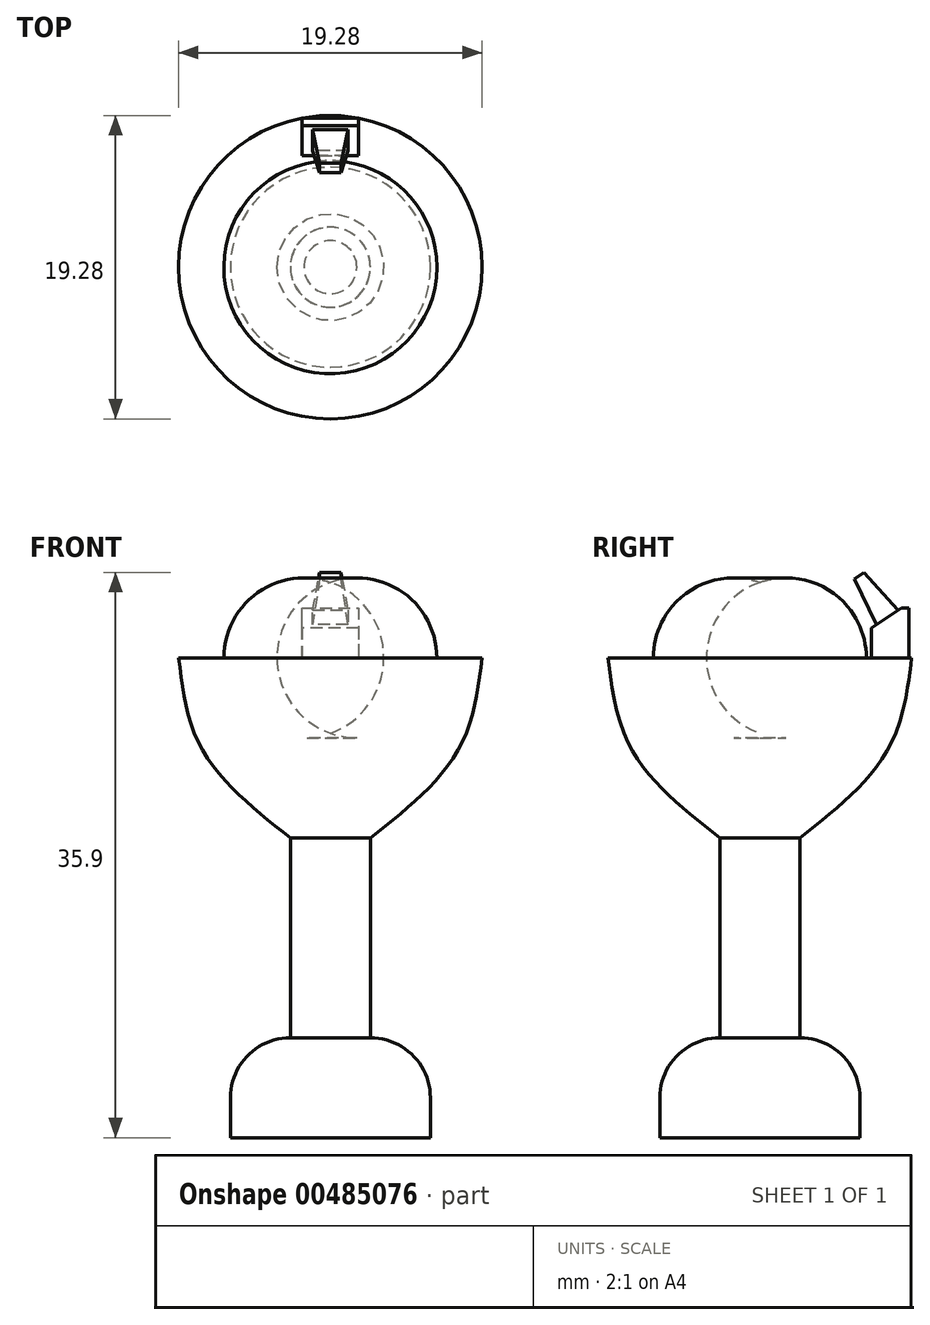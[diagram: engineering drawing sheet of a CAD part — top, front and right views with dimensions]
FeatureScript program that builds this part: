
annotation { "Feature Type Name" : "Feature", "Feature Type Description" : "" }
export const myFeature = defineFeature(function(context is Context, id is Id, definition is map)
    precondition{}
    {
        {
            var Q0;
            Q0=qCreatedBy(makeId("Top.planeOp"),FACE);
            var sketch = newSketch(context, id + "F0", { "sketchPlane" : qUnion([Q0])});
            skCircle(sketch, "E0", {"center": v(0, 0) * mm, "radius": 6.35 * mm});
            skSolve(sketch);
        }
        {
            var Q0;
            Q0 = qSketchRegion(id + "F0", true);
            extrude(context, id + "F1", {"entities" : qUnion([Q0]), "depth" : 6.35 * mm});
        }
        {
            var Q0;
            Q0=makeQuery(id+"F1.opExtrude","CAP_EDGE",EDGE,{"disambiguationData":[OSD([sQuery(id+"F0.wireOp",EDGE,"E0")])],"isStart":false});
            fillet(context, id + "F2", {"entities" : qUnion([Q0]), "radius" : 3.8 * mm, "tangentPropagation" : true, "allowEdgeOverflow" : false});
        }
        {
            var Q0;
            Q0=makeQuery(id+"F1.opExtrude","CAP_FACE",FACE,{"disambiguationData":[OSD([sQuery(id+"F0.wireOp",EDGE,"E0")])],"isStart":false});
            extrude(context, id + "F3", {"entities" : qUnion([Q0]), "operationType" : NewBodyOperationType.ADD, "depth" : 12.7 * mm});
        }
        {
            var Q0;
            Q0=qCreatedBy(makeId("Top.planeOp"),FACE);
            cPlane(context, id + "F4", {"entities" : qUnion([Q0]), "cplaneType" : CPlaneType.OFFSET, "offset" : 30.48 * mm, "width" : 152.4 * mm, "height" : 152.4 * mm});
        }
        {
            var Q0;
            Q0=qCreatedBy(id+"F4.planeOp",FACE);
            var sketch = newSketch(context, id + "F5", { "sketchPlane" : qUnion([Q0])});
            skCircle(sketch, "E1", {"center": v(0, 0) * mm, "radius": 9.64 * mm});
            skSolve(sketch);
        }
        {
            var Q0;
            Q0=qCreatedBy(makeId("Top.planeOp"),FACE);
            cPlane(context, id + "F6", {"entities" : qUnion([Q0]), "cplaneType" : CPlaneType.OFFSET, "offset" : 25.4 * mm, "width" : 152.4 * mm, "height" : 152.4 * mm});
        }
        {
            var Q0;
            Q0=qCreatedBy(id+"F6.planeOp",FACE);
            var sketch = newSketch(context, id + "F7", { "sketchPlane" : qUnion([Q0])});
            skCircle(sketch, "E2", {"center": v(0, 0) * mm, "radius": 8.51 * mm});
            skSolve(sketch);
        }
        {
            var Q0;
            Q0=makeQuery(id+"F3.opExtrude","CAP_FACE",FACE,{"disambiguationData":[OSD([sQuery(id+"F0.wireOp",EDGE,"E0")])],"isStart":false});
            var Q1;
            Q1=makeQuery(id+"F7.imprint","IMPRINT",FACE,{"disambiguationData":[TD([[makeQuery(id+"F7.imprint","IMPRINT",EDGE,{"derivedFrom":sQuery(id+"F7.wireOp",EDGE,"E2")}),1.0]])]});
            var Q2;
            Q2=makeQuery(id+"F5.imprint","IMPRINT",FACE,{"disambiguationData":[TD([[makeQuery(id+"F5.imprint","IMPRINT",EDGE,{"derivedFrom":sQuery(id+"F5.wireOp",EDGE,"E1")}),1.0]])]});
            loft(context, id + "F8", {"sheetProfilesArray" : [{ "sheetProfileEntities" : qUnion([Q0]) }, { "sheetProfileEntities" : qUnion([Q1]) }, { "sheetProfileEntities" : qUnion([Q2]) }]});
        }
        {
            var Q0;
            Q0=makeQuery(id+"F8.opLoft","CAP_FACE",FACE,{"disambiguationData":[OSD([makeQuery(id+"F5.imprint","IMPRINT",FACE,{"disambiguationData":[TD([[makeQuery(id+"F5.imprint","IMPRINT",EDGE,{"derivedFrom":sQuery(id+"F5.wireOp",EDGE,"E1")}),1.0]])]})])],"isStart":true});
            var sketch = newSketch(context, id + "F9", { "sketchPlane" : qUnion([Q0])});
            skCircle(sketch, "E3", {"center": v(0, 0) * mm, "radius": 6.76 * mm});
            skSolve(sketch);
        }
        {
            var Q0;
            Q0 = qSketchRegion(id + "F9", true);
            extrude(context, id + "F10", {"entities" : qUnion([Q0]), "operationType" : NewBodyOperationType.REMOVE, "oppositeDirection" : true, "depth" : 5.08 * mm});
        }
        {
            var Q0;
            Q0=makeQuery(id+"F10.boolean.opBoolean","COPY",EDGE,{"derivedFrom":makeQuery(id+"F10.opExtrude","CAP_EDGE",EDGE,{"disambiguationData":[OSD([sQuery(id+"F9.wireOp",EDGE,"E3")])],"isStart":false})});
            fillet(context, id + "F11", {"entities" : qUnion([Q0]), "radius" : 5.08 * mm, "tangentPropagation" : true, "allowEdgeOverflow" : false});
        }
        {
            var Q0;
            Q0=makeQuery(id+"F8.opLoft","CAP_FACE",FACE,{"disambiguationData":[OSD([makeQuery(id+"F5.imprint","IMPRINT",FACE,{"disambiguationData":[TD([[makeQuery(id+"F5.imprint","IMPRINT",EDGE,{"derivedFrom":sQuery(id+"F5.wireOp",EDGE,"E1")}),1.0]])]})])],"isStart":true});
            var sketch = newSketch(context, id + "F12", { "sketchPlane" : qUnion([Q0])});
            skLineSegment(sketch, "E4.bottom", {"start": v(-1.8, 9.47) * mm, "end": v(1.8, 9.47) * mm});
            skLineSegment(sketch, "E4.top", {"start": v(-1.8, 7.08) * mm, "end": v(1.8, 7.08) * mm});
            skLineSegment(sketch, "E4.left", {"start": v(-1.8, 9.47) * mm, "end": v(-1.8, 7.08) * mm});
            skLineSegment(sketch, "E4.right", {"start": v(1.8, 9.47) * mm, "end": v(1.8, 7.08) * mm});
            skPoint(sketch, "E4.middle", {"position": v(0, 8.27) * mm});
            skSolve(sketch);
        }
        {
            var Q0;
            Q0 = qSketchRegion(id + "F12", true);
            extrude(context, id + "F13", {"entities" : qUnion([Q0]), "operationType" : NewBodyOperationType.ADD, "depth" : 3.17 * mm});
        }
        {
            var Q0;
            Q0=makeQuery(id+"F13.opExtrude","CAP_EDGE",EDGE,{"disambiguationData":[OSD([sQuery(id+"F12.wireOp",EDGE,"E4.top")])],"isStart":false});
            chamfer(context, id + "F14", {"entities" : qUnion([Q0]), "chamferType" : ChamferType.TWO_OFFSETS, "width1" : 1.9 * mm, "oppositeDirection" : false, "width2" : 1.27 * mm, "tangentPropagation" : true});
        }
        {
            var Q0;
            Q0=makeQuery(id+"F14.opChamfer","BLEND_FACE",FACE,{"disambiguationData":[OSD([sQuery(id+"F12.wireOp",EDGE,"E4.top")])]});
            var sketch = newSketch(context, id + "F15", { "sketchPlane" : qUnion([Q0])});
            skLineSegment(sketch, "E5.bottom", {"start": v(-1.12, 25.87) * mm, "end": v(1.12, 25.87) * mm});
            skLineSegment(sketch, "E5.top", {"start": v(-1.12, 24.25) * mm, "end": v(1.12, 24.25) * mm});
            skLineSegment(sketch, "E5.left", {"start": v(-1.12, 25.87) * mm, "end": v(-1.12, 24.25) * mm});
            skLineSegment(sketch, "E5.right", {"start": v(1.12, 25.87) * mm, "end": v(1.12, 24.25) * mm});
            skPoint(sketch, "E5.middle", {"position": v(0, 25.06) * mm});
            skSolve(sketch);
        }
        {
            var Q0;
            Q0 = qSketchRegion(id + "F15", true);
            extrude(context, id + "F16", {"entities" : qUnion([Q0]), "operationType" : NewBodyOperationType.ADD, "depth" : 3.17 * mm, "hasDraft" : true, "draftAngle" : 8 * degree, "draftPullDirection" : true});
        }
    });
